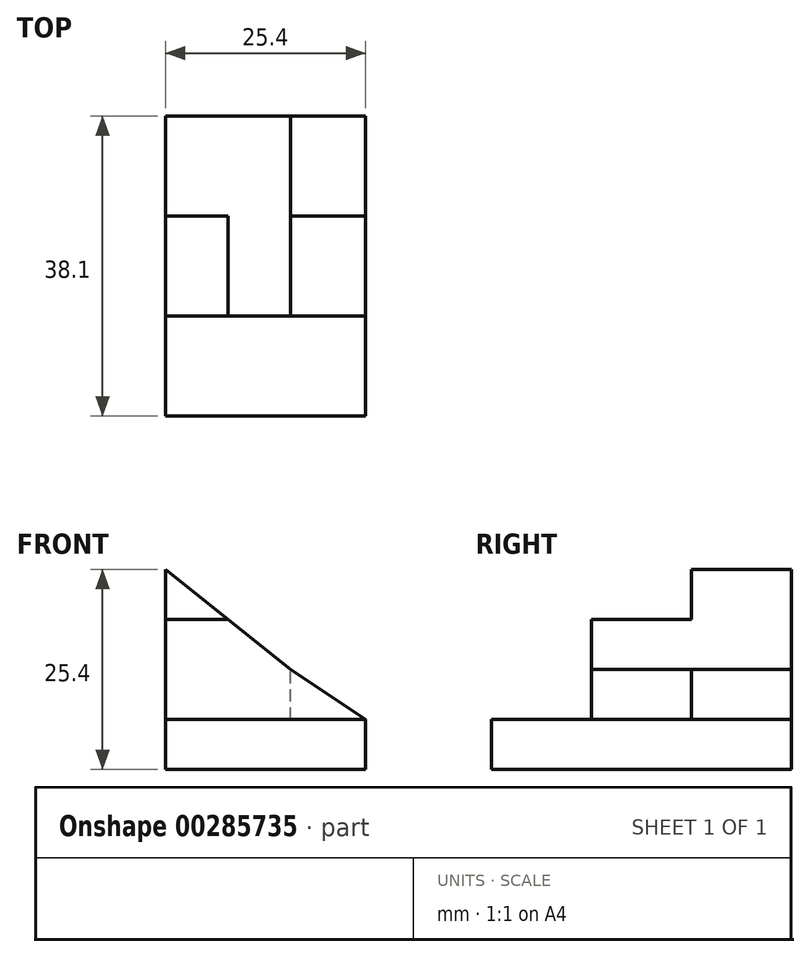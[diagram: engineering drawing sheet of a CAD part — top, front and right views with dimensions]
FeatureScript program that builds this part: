
annotation { "Feature Type Name" : "Feature", "Feature Type Description" : "" }
export const myFeature = defineFeature(function(context is Context, id is Id, definition is map)
    precondition{}
    {
        {
            var Q0;
            Q0=qCreatedBy(makeId("Front.planeOp"),FACE);
            var sketch = newSketch(context, id + "F0", { "sketchPlane" : qUnion([Q0])});
            skLineSegment(sketch, "E0", {"start": v(0, 0) * mm, "end": v(0, 6.35) * mm});
            skLineSegment(sketch, "E1", {"start": v(0, 6.35) * mm, "end": v(25.4, 6.35) * mm});
            skLineSegment(sketch, "E2", {"start": v(25.4, 6.35) * mm, "end": v(25.4, 0) * mm});
            skLineSegment(sketch, "E3", {"start": v(25.4, 0) * mm, "end": v(0, 0) * mm});
            skSolve(sketch);
        }
        {
            var Q0;
            Q0 = qSketchRegion(id + "F0", true);
            extrude(context, id + "F1", {"entities" : qUnion([Q0]), "depth" : 38.1 * mm});
        }
        {
            var Q0;
            Q0=qCreatedBy(makeId("Front.planeOp"),FACE);
            var sketch = newSketch(context, id + "F2", { "sketchPlane" : qUnion([Q0])});
            skLineSegment(sketch, "E4", {"start": v(0, 6.35) * mm, "end": v(0, 19.05) * mm});
            skLineSegment(sketch, "E5", {"start": v(0, 19.05) * mm, "end": v(7.94, 19.05) * mm});
            skLineSegment(sketch, "E6", {"start": v(7.94, 19.05) * mm, "end": v(15.88, 12.7) * mm});
            skLineSegment(sketch, "E7", {"start": v(15.88, 12.7) * mm, "end": v(15.88, 6.35) * mm});
            skLineSegment(sketch, "E8", {"start": v(15.88, 6.35) * mm, "end": v(0, 6.35) * mm});
            skLineSegment(sketch, "E9", {"start": v(0, 19.05) * mm, "end": v(0, 25.4) * mm});
            skLineSegment(sketch, "E10", {"start": v(0, 25.4) * mm, "end": v(7.94, 19.05) * mm});
            skSolve(sketch);
        }
        {
            var Q0;
            Q0=makeQuery(id+"F2.imprint","IMPRINT",FACE,{"disambiguationData":[TD([[makeQuery(id+"F2.imprint","IMPRINT",EDGE,{"derivedFrom":sQuery(id+"F2.wireOp",EDGE,"E4")}),-1.0]])]});
            extrude(context, id + "F3", {"entities" : qUnion([Q0]), "operationType" : NewBodyOperationType.ADD, "depth" : 25.4 * mm});
        }
        {
            var Q0;
            Q0=makeQuery(id+"F2.imprint","IMPRINT",FACE,{"disambiguationData":[TD([[makeQuery(id+"F2.imprint","IMPRINT",EDGE,{"derivedFrom":sQuery(id+"F2.wireOp",EDGE,"E5")}),1.0]])]});
            extrude(context, id + "F4", {"entities" : qUnion([Q0]), "operationType" : NewBodyOperationType.ADD, "depth" : 12.7 * mm});
        }
        {
            var Q0;
            Q0=qCreatedBy(makeId("Front.planeOp"),FACE);
            var sketch = newSketch(context, id + "F5", { "sketchPlane" : qUnion([Q0])});
            skLineSegment(sketch, "E11", {"start": v(15.88, 12.7) * mm, "end": v(25.4, 6.35) * mm});
            skLineSegment(sketch, "E12", {"start": v(25.4, 6.35) * mm, "end": v(15.88, 6.35) * mm});
            skLineSegment(sketch, "E13", {"start": v(15.88, 6.35) * mm, "end": v(15.88, 12.7) * mm});
            skSolve(sketch);
        }
        {
            var Q0;
            Q0 = qSketchRegion(id + "F5", true);
            extrude(context, id + "F6", {"entities" : qUnion([Q0]), "operationType" : NewBodyOperationType.ADD, "depth" : 25.4 * mm});
        }
        {
            var Q0;
            Q0 = qSketchRegion(id + "F5", true);
            extrude(context, id + "F7", {"entities" : qUnion([Q0]), "operationType" : NewBodyOperationType.REMOVE, "depth" : 12.7 * mm});
        }
    });
